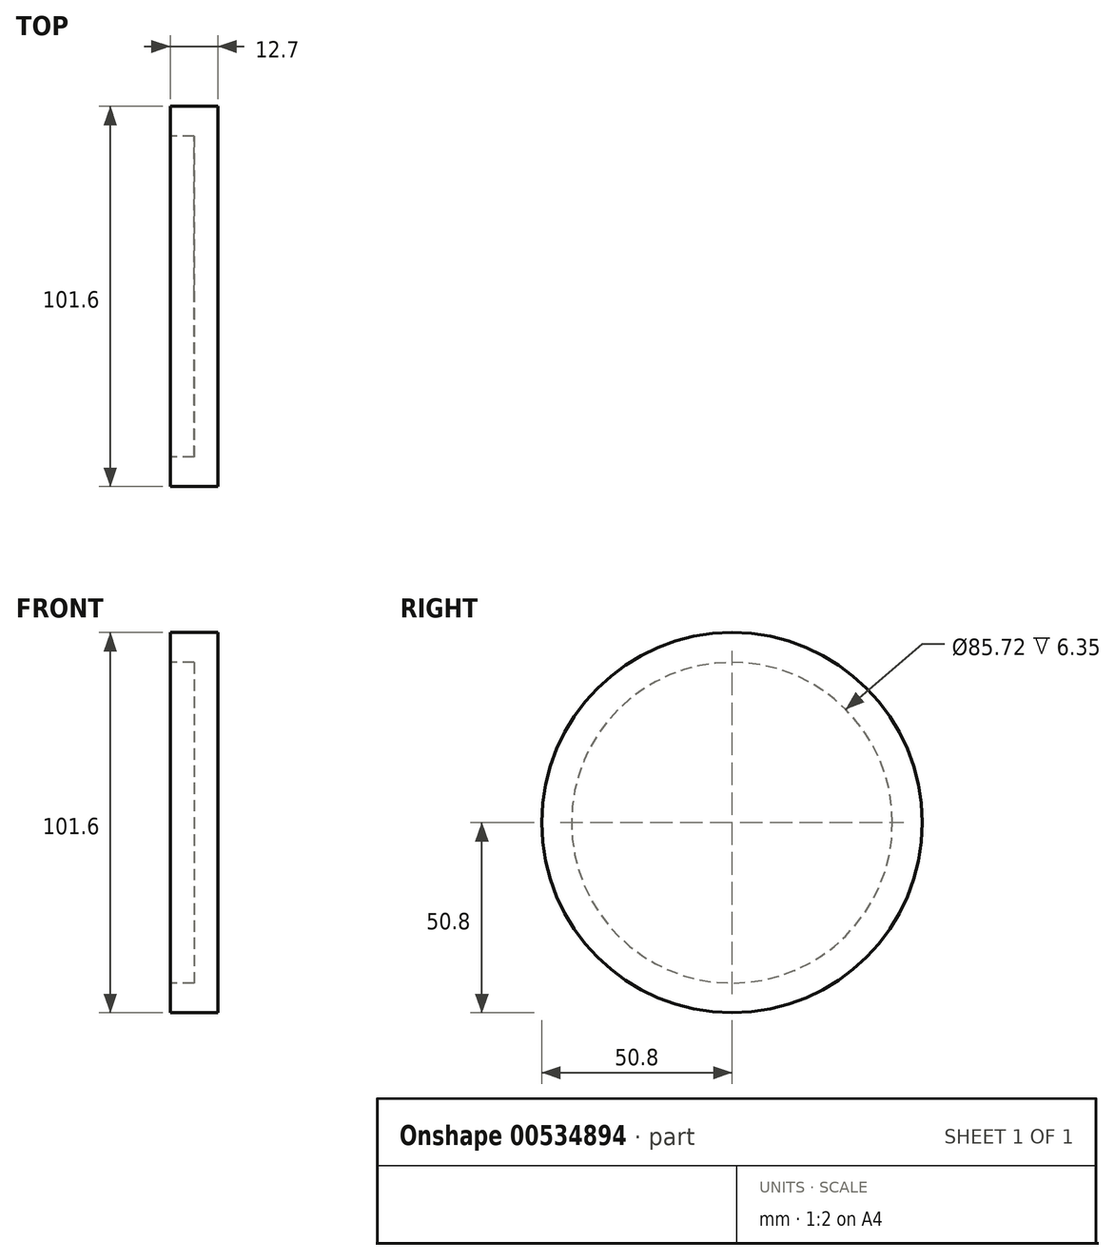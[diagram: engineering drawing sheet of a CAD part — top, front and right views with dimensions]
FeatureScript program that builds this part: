
annotation { "Feature Type Name" : "Feature", "Feature Type Description" : "" }
export const myFeature = defineFeature(function(context is Context, id is Id, definition is map)
    precondition{}
    {
        {
            var Q0;
            Q0=qCreatedBy(makeId("Right.planeOp"),FACE);
            var sketch = newSketch(context, id + "F0", { "sketchPlane" : qUnion([Q0])});
            skCircle(sketch, "E0", {"center": v(0, 0) * mm, "radius": 50.8 * mm});
            skSolve(sketch);
        }
        {
            var Q0;
            Q0 = qSketchRegion(id + "F0", true);
            extrude(context, id + "F1", {"entities" : qUnion([Q0]), "depth" : 12.7 * mm, "offsetDistance" : 25.4 * mm});
        }
        {
            var Q0;
            Q0=makeQuery(id+"F1.opExtrude","CAP_FACE",FACE,{"disambiguationData":[OSD([sQuery(id+"F0.wireOp",EDGE,"E0")])],"isStart":true});
            var sketch = newSketch(context, id + "F2", { "sketchPlane" : qUnion([Q0])});
            skCircle(sketch, "E1", {"center": v(0, 0) * mm, "radius": 42.86 * mm});
            skSolve(sketch);
        }
        {
            var Q0;
            Q0 = qSketchRegion(id + "F2", true);
            extrude(context, id + "F3", {"entities" : qUnion([Q0]), "operationType" : NewBodyOperationType.REMOVE, "oppositeDirection" : true, "depth" : 6.35 * mm, "offsetDistance" : 25.4 * mm});
        }
    });
